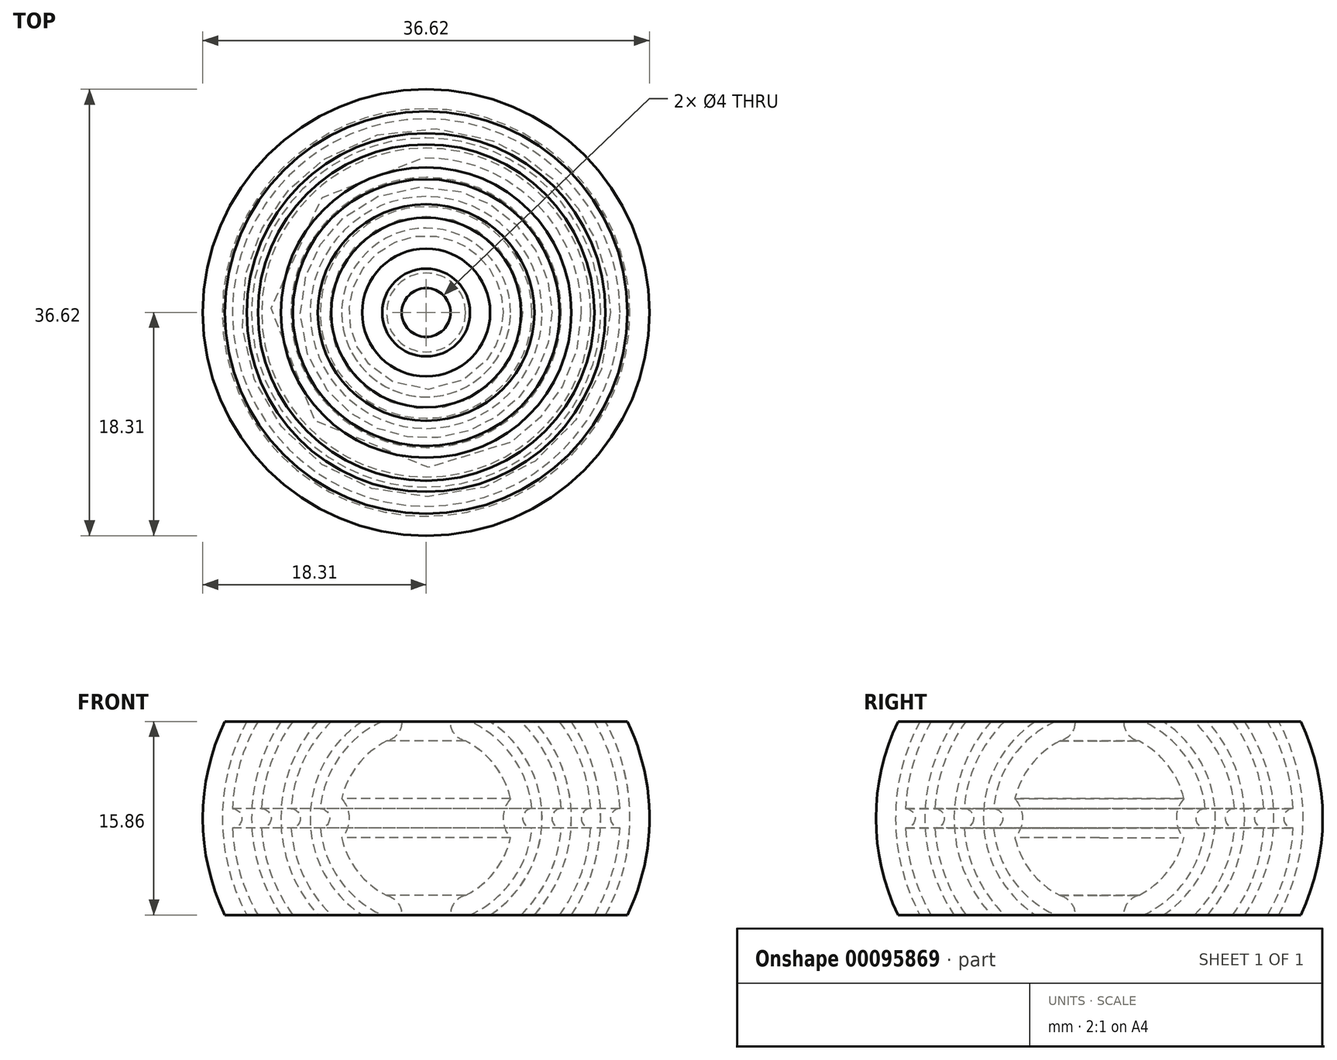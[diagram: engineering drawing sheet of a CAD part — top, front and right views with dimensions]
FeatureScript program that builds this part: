
annotation { "Feature Type Name" : "Feature", "Feature Type Description" : "" }
export const myFeature = defineFeature(function(context is Context, id is Id, definition is map)
    precondition{}
    {
        {
            assignVariable(context, id + "F0", {"name" : "Wall", "anyValue" : 0.4 * 4});
        }
        {
            var Q0;
            Q0=qCreatedBy(makeId("Front.planeOp"),FACE);
            var sketch = newSketch(context, id + "F1", { "sketchPlane" : qUnion([Q0])});
            skCircle(sketch, "E0", {"center": v(0, 0) * mm, "radius": 8.71 * mm});
            skCircle(sketch, "E1", {"center": v(0, 0) * mm, "radius": 9.51 * mm});
            skCircle(sketch, "E2", {"center": v(0, 0) * mm, "radius": 11.11 * mm});
            skCircle(sketch, "E3", {"center": v(0, 0) * mm, "radius": 11.91 * mm});
            skCircle(sketch, "E4", {"center": v(0, 0) * mm, "radius": 13.51 * mm});
            skCircle(sketch, "E5", {"center": v(0, 0) * mm, "radius": 14.31 * mm});
            skCircle(sketch, "E6", {"center": v(0, 0) * mm, "radius": 15.91 * mm});
            skPoint(sketch, "E7", {"position": v(-14.31, 0) * mm});
            skPoint(sketch, "E8", {"position": v(-11.91, 0) * mm});
            skPoint(sketch, "E9", {"position": v(-9.51, 0) * mm});
            skPoint(sketch, "E10", {"position": v(-15.91, 0) * mm});
            skPoint(sketch, "E11", {"position": v(-13.51, 0) * mm});
            skPoint(sketch, "E12", {"position": v(-11.11, 0) * mm});
            skPoint(sketch, "E13", {"position": v(-8.71, 0) * mm});
            skLineSegment(sketch, "E14", {"start": v(0, 7.93) * mm, "end": v(-32.85, 7.93) * mm});
            skPoint(sketch, "E15", {"position": v(-5.25, 7.93) * mm});
            skPoint(sketch, "E16", {"position": v(-8.89, 7.93) * mm});
            skPoint(sketch, "E17", {"position": v(-11.91, 7.93) * mm});
            skPoint(sketch, "E18", {"position": v(-3.6, 7.93) * mm});
            skLineSegment(sketch, "E19", {"start": v(0, 30.27) * mm, "end": v(0, -32.82) * mm});
            skLineSegment(sketch, "E20.MirrorCS", {"start": v(0, -7.93) * mm, "end": v(-32.85, -7.93) * mm});
            skLineSegment(sketch, "E21", {"start": v(-2, 7.93) * mm, "end": v(-2, -7.93) * mm});
            skCircle(sketch, "E22", {"center": v(0, 0) * mm, "radius": 2 * mm});
            skLineSegment(sketch, "E23", {"start": v(0, 2.88) * mm, "end": v(-1.44, 1.39) * mm});
            skLineSegment(sketch, "E24.MirrorCS", {"start": v(0, 2.88) * mm, "end": v(1.44, 1.39) * mm});
            skLineSegment(sketch, "E25.MirrorCS", {"start": v(0, -2.88) * mm, "end": v(-1.44, -1.39) * mm});
            skLineSegment(sketch, "E26.MirrorCS", {"start": v(0, -2.88) * mm, "end": v(1.44, -1.39) * mm});
            skPoint(sketch, "E27", {"position": v(-9.51, 7.17) * mm});
            skPoint(sketch, "E28", {"position": v(-7.11, 6.32) * mm});
            skCircle(sketch, "E29", {"center": v(0, 0) * mm, "radius": 16.71 * mm});
            skCircle(sketch, "E30", {"center": v(0, 0) * mm, "radius": 18.31 * mm});
            skCircle(sketch, "E31", {"center": v(-8.71, 0) * mm, "radius": 0.8 * mm});
            skCircle(sketch, "E32", {"center": v(-11.11, 0) * mm, "radius": 0.8 * mm});
            skCircle(sketch, "E33", {"center": v(-13.51, 0) * mm, "radius": 0.8 * mm});
            skCircle(sketch, "E34", {"center": v(-15.91, 0) * mm, "radius": 0.8 * mm});
            skSolve(sketch);
        }
        {
            var Q0;
            {var subQ3=sQuery(id+"F1.wireOp",EDGE,"E0");var subQ5=sQuery(id+"F1.wireOp",EDGE,"E14");var subQ7=makeQuery(id+"F1.imprint","INTERSECT",VERTEX,{"derivedFrom":[subQ3,subQ5]});Q0=makeQuery(id+"F1.imprint","IMPRINT",FACE,{"disambiguationData":[TD([[makeQuery(id+"F1.imprint","IMPRINT",EDGE,{"disambiguationData":[TD([[subQ7,-1.0]])],"derivedFrom":subQ3}),1.0]])]});}
            var Q1;
            {var subQ5=sQuery(id+"F1.wireOp",EDGE,"E14");var subQ6=sQuery(id+"F1.wireOp",EDGE,"E1");var subQ7=makeQuery(id+"F1.imprint","INTERSECT",VERTEX,{"derivedFrom":[subQ6,subQ5]});Q1=makeQuery(id+"F1.imprint","IMPRINT",FACE,{"disambiguationData":[TD([[makeQuery(id+"F1.imprint","IMPRINT",EDGE,{"disambiguationData":[TD([[subQ7,-1.0]])],"derivedFrom":subQ6}),-1.0]])]});}
            var Q2;
            {var subQ5=sQuery(id+"F1.wireOp",EDGE,"E14");var subQ6=sQuery(id+"F1.wireOp",EDGE,"E3");var subQ7=makeQuery(id+"F1.imprint","INTERSECT",VERTEX,{"derivedFrom":[subQ6,subQ5]});Q2=makeQuery(id+"F1.imprint","IMPRINT",FACE,{"disambiguationData":[TD([[makeQuery(id+"F1.imprint","IMPRINT",EDGE,{"disambiguationData":[TD([[subQ7,-1.0]])],"derivedFrom":subQ6}),-1.0]])]});}
            var Q3;
            {var subQ5=sQuery(id+"F1.wireOp",EDGE,"E14");var subQ8=sQuery(id+"F1.wireOp",EDGE,"E5");var subQ11=makeQuery(id+"F1.imprint","INTERSECT",VERTEX,{"derivedFrom":[subQ8,subQ5]});Q3=makeQuery(id+"F1.imprint","IMPRINT",FACE,{"disambiguationData":[TD([[makeQuery(id+"F1.imprint","IMPRINT",EDGE,{"disambiguationData":[TD([[subQ11,-1.0]])],"derivedFrom":subQ8}),-1.0]])]});}
            var Q4;
            {var subQ4=sQuery(id+"F1.wireOp",EDGE,"E14");var subQ6=sQuery(id+"F1.wireOp",EDGE,"E30");var subQ8=makeQuery(id+"F1.imprint","INTERSECT",VERTEX,{"derivedFrom":[subQ4,subQ6]});Q4=makeQuery(id+"F1.imprint","IMPRINT",FACE,{"disambiguationData":[TD([[makeQuery(id+"F1.imprint","IMPRINT",EDGE,{"disambiguationData":[TD([[subQ8,1.0]])],"derivedFrom":subQ4}),1.0]])]});}
            var Q5;
            Q5=sQuery(id+"F1.wireOp",EDGE,"E19");
            revolve(context, id + "F2", {"entities" : qUnion([Q0, Q1, Q2, Q3, Q4]), "axis" : qUnion([Q5]), "revolveType" : RevolveType.FULL});
        }
        {
            var Q0;
            Q0=makeQuery(id+"F2.opRevolve","SWEPT_FACE",FACE,{"disambiguationData":[OSD([sQuery(id+"F1.wireOp",EDGE,"E21")])]});
            shell(context, id + "F3", {"entities" : qUnion([Q0]), "thickness" : (getVariable(context, 'Wall')) * mm});
        }
        {
            var Q0;
            Q0=makeQuery(id+"F3.opShell","OFFSET_EDGE",EDGE,{"disambiguationData":[OSD([sQuery(id+"F1.wireOp",EDGE,"E20.MirrorCS"),sQuery(id+"F1.wireOp",EDGE,"E21")])]});
            var Q1;
            Q1=makeQuery(id+"F3.opShell","OFFSET_EDGE",EDGE,{"disambiguationData":[OSD([sQuery(id+"F1.wireOp",EDGE,"E14"),sQuery(id+"F1.wireOp",EDGE,"E21")])]});
            fillet(context, id + "F4", {"entities" : qUnion([Q0, Q1]), "radius" : (getVariable(context, 'Wall')) * mm, "tangentPropagation" : true, "allowEdgeOverflow" : false});
        }
    });
